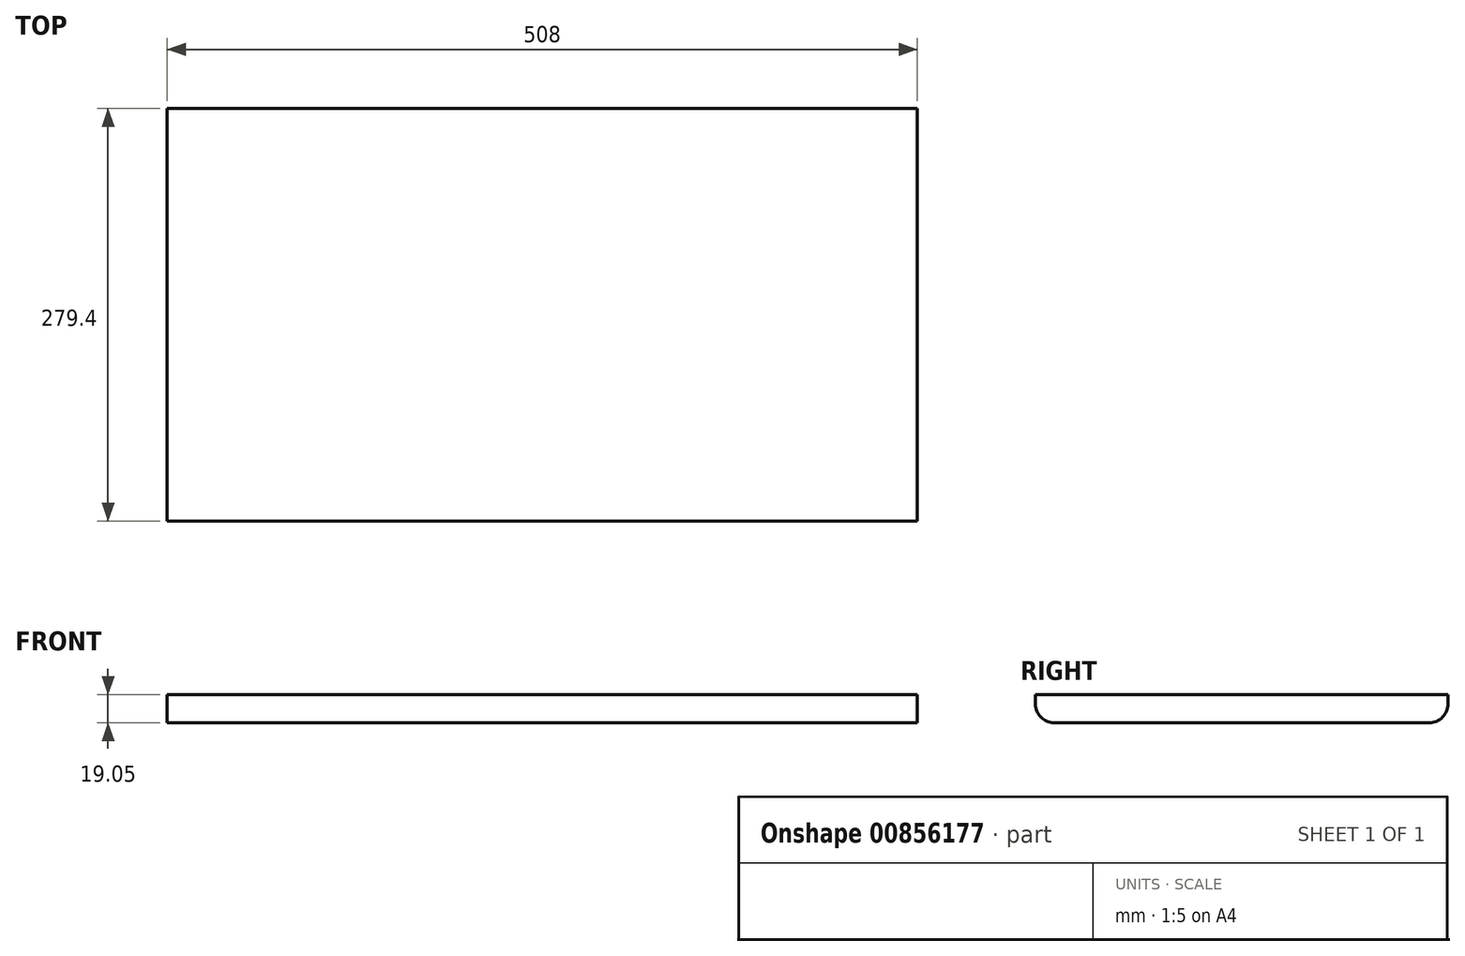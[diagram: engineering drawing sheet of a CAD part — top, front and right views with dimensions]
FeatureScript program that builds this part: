
annotation { "Feature Type Name" : "Feature", "Feature Type Description" : "" }
export const myFeature = defineFeature(function(context is Context, id is Id, definition is map)
    precondition{}
    {
        {
            var Q0;
            Q0=qCreatedBy(makeId("Top.planeOp"),FACE);
            var sketch = newSketch(context, id + "F0", { "sketchPlane" : qUnion([Q0])});
            skLineSegment(sketch, "E0.bottom", {"start": v(-508, 279.4) * mm, "end": v(0, 279.4) * mm});
            skLineSegment(sketch, "E0.top", {"start": v(-508, 0) * mm, "end": v(0, 0) * mm});
            skLineSegment(sketch, "E0.left", {"start": v(-508, 279.4) * mm, "end": v(-508, 0) * mm});
            skLineSegment(sketch, "E0.right", {"start": v(0, 279.4) * mm, "end": v(0, 0) * mm});
            skSolve(sketch);
        }
        {
            var Q0;
            Q0 = qSketchRegion(id + "F0", true);
            extrude(context, id + "F1", {"entities" : qUnion([Q0]), "depth" : 19.05 * mm, "offsetDistance" : 25.4 * mm});
        }
        {
            var Q0;
            Q0=makeQuery(id+"F1.opExtrude","CAP_EDGE",EDGE,{"disambiguationData":[OSD([sQuery(id+"F0.wireOp",EDGE,"E0.top")])],"isStart":true});
            var Q1;
            Q1=makeQuery(id+"F1.opExtrude","CAP_EDGE",EDGE,{"disambiguationData":[OSD([sQuery(id+"F0.wireOp",EDGE,"E0.bottom")])],"isStart":true});
            fillet(context, id + "F2", {"entities" : qUnion([Q0, Q1]), "radius" : 12.7 * mm, "tangentPropagation" : true, "allowEdgeOverflow" : false});
        }
    });
